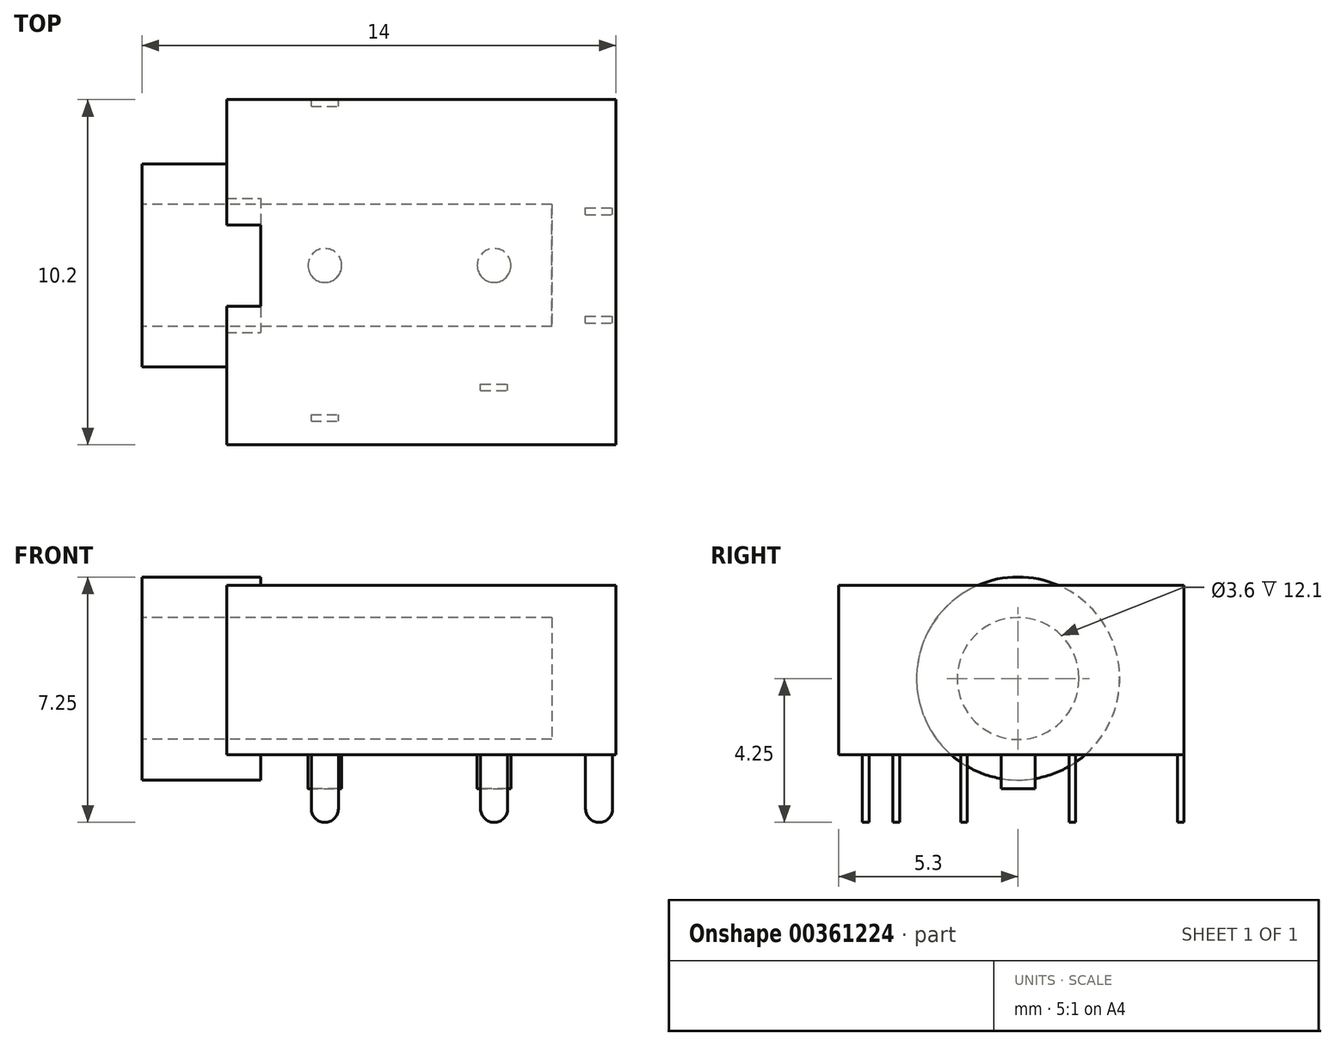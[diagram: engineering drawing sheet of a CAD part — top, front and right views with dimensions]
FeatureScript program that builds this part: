
annotation { "Feature Type Name" : "Feature", "Feature Type Description" : "" }
export const myFeature = defineFeature(function(context is Context, id is Id, definition is map)
    precondition{}
    {
        {
            var Q0;
            Q0=qCreatedBy(makeId("Top.planeOp"),FACE);
            var sketch = newSketch(context, id + "F0", { "sketchPlane" : qUnion([Q0])});
            skLineSegment(sketch, "E0.bottom", {"start": v(0, 4.9) * mm, "end": v(11.5, 4.9) * mm});
            skLineSegment(sketch, "E0.top", {"start": v(0, -5.3) * mm, "end": v(11.5, -5.3) * mm});
            skLineSegment(sketch, "E0.left", {"start": v(0, 4.9) * mm, "end": v(0, -5.3) * mm});
            skLineSegment(sketch, "E0.right", {"start": v(11.5, 4.9) * mm, "end": v(11.5, -5.3) * mm});
            skSolve(sketch);
        }
        {
            var Q0;
            Q0=qSketchRegion(id+"F0",true);
            extrude(context, id + "F1", {"entities" : qUnion([Q0]), "depth" : 5 * mm});
        }
        {
            var Q0;
            Q0=makeQuery(id+"F1.opExtrude","SWEPT_FACE",FACE,{"disambiguationData":[OSD([sQuery(id+"F0.wireOp",EDGE,"E0.left")])]});
            var sketch = newSketch(context, id + "F2", { "sketchPlane" : qUnion([Q0])});
            skCircle(sketch, "E1", {"center": v(0, 2.25) * mm, "radius": 3 * mm});
            skSolve(sketch);
        }
        {
            var Q0;
            Q0=qSketchRegion(id+"F2",true);
            extrude(context, id + "F3", {"entities" : qUnion([Q0]), "operationType" : NewBodyOperationType.ADD, "depth" : 2.5 * mm, "hasSecondDirection" : true, "secondDirectionOppositeDirection" : true, "secondDirectionDepth" : 1 * mm});
        }
        {
            var Q0;
            Q0=makeQuery(id+"F3.opExtrude","CAP_FACE",FACE,{"disambiguationData":[OSD([sQuery(id+"F2.wireOp",EDGE,"E1")])],"isStart":false});
            var sketch = newSketch(context, id + "F4", { "sketchPlane" : qUnion([Q0])});
            skCircle(sketch, "E2", {"center": v(0, 2.25) * mm, "radius": 1.8 * mm});
            skSolve(sketch);
        }
        {
            var Q0;
            Q0=qSketchRegion(id+"F4",true);
            extrude(context, id + "F5", {"entities" : qUnion([Q0]), "operationType" : NewBodyOperationType.REMOVE, "oppositeDirection" : true, "depth" : 12.1 * mm});
        }
        {
            var Q0;
            Q0=makeQuery(id+"F1.opExtrude","CAP_FACE",FACE,{"disambiguationData":[OSD([sQuery(id+"F0.wireOp",EDGE,"E0.bottom"),sQuery(id+"F0.wireOp",EDGE,"E0.top"),sQuery(id+"F0.wireOp",EDGE,"E0.left"),sQuery(id+"F0.wireOp",EDGE,"E0.right")])],"isStart":true});
            var sketch = newSketch(context, id + "F6", { "sketchPlane" : qUnion([Q0])});
            skCircle(sketch, "E3", {"center": v(2.9, 0) * mm, "radius": 0.5 * mm});
            skCircle(sketch, "E4", {"center": v(7.9, 0) * mm, "radius": 0.5 * mm});
            skSolve(sketch);
        }
        {
            var Q0;
            Q0=qSketchRegion(id+"F6",true);
            extrude(context, id + "F7", {"entities" : qUnion([Q0]), "operationType" : NewBodyOperationType.ADD, "depth" : 1 * mm});
        }
        {
            var Q0;
            Q0=qCreatedBy(makeId("Front.planeOp"),FACE);
            var sketch = newSketch(context, id + "F8", { "sketchPlane" : qUnion([Q0])});
            skLineSegment(sketch, "E5.bottom", {"start": v(-0.4, 0) * mm, "end": v(0.4, 0) * mm});
            skLineSegment(sketch, "E5.top", {"start": v(0, -2) * mm, "end": v(0, -2) * mm});
            skLineSegment(sketch, "E5.left", {"start": v(-0.4, 0) * mm, "end": v(-0.4, -1.6) * mm});
            skLineSegment(sketch, "E5.right", {"start": v(0.4, 0) * mm, "end": v(0.4, -1.6) * mm});
            skPoint(sketch, "E6.visualSharp", {"position": v(-0.4, -2) * mm});
            skArc(sketch, "E6.filletArc", {"start": v(-0.4, -1.6) * mm, "mid": v(-0.28, -1.88) * mm, "end": v(0, -2) * mm});
            skPoint(sketch, "E7.visualSharp", {"position": v(0.4, -2) * mm});
            skArc(sketch, "E7.filletArc", {"start": v(0, -2) * mm, "mid": v(0.28, -1.88) * mm, "end": v(0.4, -1.6) * mm});
            skPoint(sketch, "E8", {"position": v(0, 0) * mm});
            skSolve(sketch);
        }
        {
            var Q0;
            Q0=qSketchRegion(id+"F8",true);
            extrude(context, id + "F9", {"entities" : qUnion([Q0]), "depth" : 0.2 * mm, "symmetric" : true});
        }
        {
            var Q0;
            Q0=makeQuery(id+"F9.opExtrude","SWEPT_BODY",BODY,{"disambiguationData":[OSD([sQuery(id+"F8.wireOp",EDGE,"E5.bottom"),sQuery(id+"F8.wireOp",EDGE,"E5.left"),sQuery(id+"F8.wireOp",EDGE,"E5.right"),sQuery(id+"F8.wireOp",EDGE,"E6.filletArc"),sQuery(id+"F8.wireOp",EDGE,"E7.filletArc")])]});
            transform(context, id + "F10", {"entities" : qUnion([Q0]), "transformType" : TransformType.TRANSLATION_3D, "dx" : 2.9 * mm, "dy" : 4.8 * mm, "dz" : 0 * mm, "makeCopy" : true});
        }
        {
            var Q0;
            Q0=makeQuery(id+"F9.opExtrude","SWEPT_BODY",BODY,{"disambiguationData":[OSD([sQuery(id+"F8.wireOp",EDGE,"E5.bottom"),sQuery(id+"F8.wireOp",EDGE,"E5.left"),sQuery(id+"F8.wireOp",EDGE,"E5.right"),sQuery(id+"F8.wireOp",EDGE,"E6.filletArc"),sQuery(id+"F8.wireOp",EDGE,"E7.filletArc")])]});
            transform(context, id + "F11", {"entities" : qUnion([Q0]), "transformType" : TransformType.TRANSLATION_3D, "dx" : 2.9 * mm, "dy" : -4.5 * mm, "dz" : 0 * mm, "makeCopy" : true});
        }
        {
            var Q0;
            Q0=makeQuery(id+"F9.opExtrude","SWEPT_BODY",BODY,{"disambiguationData":[OSD([sQuery(id+"F8.wireOp",EDGE,"E5.bottom"),sQuery(id+"F8.wireOp",EDGE,"E5.left"),sQuery(id+"F8.wireOp",EDGE,"E5.right"),sQuery(id+"F8.wireOp",EDGE,"E6.filletArc"),sQuery(id+"F8.wireOp",EDGE,"E7.filletArc")])]});
            transform(context, id + "F12", {"entities" : qUnion([Q0]), "transformType" : TransformType.TRANSLATION_3D, "dx" : 11 * mm, "dy" : 1.6 * mm, "dz" : 0 * mm, "makeCopy" : true});
        }
        {
            var Q0;
            Q0=makeQuery(id+"F9.opExtrude","SWEPT_BODY",BODY,{"disambiguationData":[OSD([sQuery(id+"F8.wireOp",EDGE,"E5.bottom"),sQuery(id+"F8.wireOp",EDGE,"E5.left"),sQuery(id+"F8.wireOp",EDGE,"E5.right"),sQuery(id+"F8.wireOp",EDGE,"E6.filletArc"),sQuery(id+"F8.wireOp",EDGE,"E7.filletArc")])]});
            transform(context, id + "F13", {"entities" : qUnion([Q0]), "transformType" : TransformType.TRANSLATION_3D, "dx" : 11 * mm, "dy" : -1.6 * mm, "dz" : 0 * mm, "makeCopy" : true});
        }
        {
            var Q0;
            Q0=makeQuery(id+"F9.opExtrude","SWEPT_BODY",BODY,{"disambiguationData":[OSD([sQuery(id+"F8.wireOp",EDGE,"E5.bottom"),sQuery(id+"F8.wireOp",EDGE,"E5.left"),sQuery(id+"F8.wireOp",EDGE,"E5.right"),sQuery(id+"F8.wireOp",EDGE,"E6.filletArc"),sQuery(id+"F8.wireOp",EDGE,"E7.filletArc")])]});
            transform(context, id + "F14", {"entities" : qUnion([Q0]), "transformType" : TransformType.TRANSLATION_3D, "dx" : 7.9 * mm, "dy" : -3.6 * mm, "dz" : 0 * mm, "makeCopy" : false});
        }
    });
